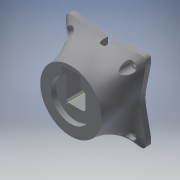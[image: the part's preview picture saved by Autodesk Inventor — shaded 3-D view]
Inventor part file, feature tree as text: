
AUTODESK INVENTOR PART (.ipt)
format: ipt  version: 2018 (Build 220112000, 112)  size: 1,945,600 bytes
history: native  units: mm
features: sketch x37, projected_geometry x36, extrude x32, fillet x13, hole x4, chamfer x4, mirror x1, other x1, revolve x1, shell x1, pattern_circular x1
ambient origin geometry x8: Origin, YZ Plane, XZ Plane, XY Plane, X Axis, Y Axis, Z Axis, Center Point
bodies: Solid1 (feature_tree)
feature tree (131):
  extrude  "Extrusion1"  Depth=45.0mm
  extrude  "Extrusion2"  Depth=2.25mm
  hole  "Hole1"  [1 undecoded]
  hole  "Hole2"  [1 undecoded]
  fillet  "Fillet1"  Radius=14.0mm
  extrude  "Extrusion3"  Depth=18.5mm
  extrude  "Extrusion4"  Depth=10.0mm
  extrude  "Extrusion5"  Depth=2.195mm
  extrude  "Extrusion6"  Depth=20.5mm
  hole  "Hole3"  [1 undecoded]
  extrude  "Extrusion7"  Depth=0.5mm
  extrude  "Extrusion8"  Depth=5.0mm TaperAngle=0.0deg
  extrude  "Extrusion9"  Depth=10.0mm
  extrude  "Extrusion10"  Depth=10.0mm
  extrude  "Extrusion11"  Depth=14.5mm
  extrude  "Extrusion12"  Depth=14.5mm
  extrude  "Extrusion13"  Depth=5.0mm
  extrude  "Extrusion14"  Depth=2.25mm
  extrude  "Extrusion15"  Depth=5.0mm
  extrude  "Extrusion16"  Depth=9.0mm
  extrude  "Extrusion17"  Depth=4.0mm
  chamfer  "Chamfer1"  Distance=1.0mm
  fillet  "Fillet7"  Radius=20.7mm
  fillet  "Fillet8"  Radius=32.0mm
  mirror  "Mirror1"
  extrude  "Extrusion18"  Depth=1.0mm TaperAngle=0.0deg
  extrude  "Extrusion19"  Depth=8.0mm
  extrude  "Extrusion20"  Depth=0.2mm TaperAngle=0.0deg
  extrude  "Extrusion21"  Depth=0.5mm TaperAngle=0.0deg
  extrude  "Extrusion22"  Depth=3.0mm TaperAngle=0.0deg
  extrude  "Extrusion23"  Depth=0.2mm TaperAngle=0.0deg
  extrude  "Extrusion24"  Depth=2.5mm TaperAngle=45.0deg
  sketch  "Sketch35"  dims[d91=8.0mm d92=0.0mm d93=3.0mm d94=0.0mm]
  other  "Work Axis1"
  revolve  "Revolution1"  [1 undecoded]
  extrude  "Extrusion25"  Depth=4.0mm TaperAngle=0.0deg
  extrude  "Extrusion26"  Depth=19.2mm TaperAngle=0.0deg
  shell  "Shell1"  Thickness=52.1mm
  extrude  "Extrusion27"  Depth=9.0mm
  extrude  "Extrusion28"  Depth=25.0mm
  chamfer  "Chamfer4"  Distance=6.9mm
  chamfer  "Chamfer5"  Distance=5.2mm
  extrude  "Extrusion29"  Depth=5.2mm
  pattern_circular  "Circular Pattern1"  [2 undecoded]
  fillet  "Fillet11"  Radius=5.0mm
  fillet  "Fillet12"  [1 undecoded]
  fillet  "Fillet13"  Radius=5.0mm
  fillet  "Fillet14"  Radius=105.0mm
  chamfer  "Chamfer6"  Distance=105.0mm
  hole  "Hole6"  [1 undecoded]
  extrude  "Extrusion30"  Depth=0.3mm
  fillet  "Fillet15"  Radius=12.8mm
  extrude  "Extrusion31"  Depth=0.3mm
  fillet  "Fillet16"  Radius=12.8mm
  extrude  "Extrusion32"  Depth=0.3mm
  fillet  "Fillet17"  Radius=20.0mm
  fillet  "Fillet18"  Radius=20.0mm
  fillet  "Fillet19"  Radius=6.0mm
  fillet  "Fillet20"  Radius=40.0mm
  sketch  "Sketch1"  dims[d0=24.5mm d1=45.0mm]
  sketch  "Sketch2"  dims[d2=1.95mm d3=0.0mm d4=2.25mm]
  projected_geometry  "Projected Loop1"
  sketch  "Sketch3"  dims[d5=20.0mm d6=2.25mm]
  projected_geometry  "Projected Loop2"
  sketch  "Sketch4"  dims[d7=5.25mm d8=5.25mm d9=14.0mm]
  projected_geometry  "Projected Loop3"
  sketch  "Sketch5"  dims[d10=5.25mm d11=18.5mm]
  projected_geometry  "Projected Loop4"
  sketch  "Sketch6"  dims[d12=10.0mm d13=0.0mm d14=20.5mm]
  projected_geometry  "Projected Loop5"
  sketch  "Sketch7"  dims[d15=2.0mm d16=2.195mm]
  projected_geometry  "Projected Loop6"
  sketch  "Sketch8"  dims[d17=2.0mm]
  projected_geometry  "Projected Loop7"
  sketch  "Sketch9"  dims[d18=2.4mm d19=6.0mm d20=4.4mm d21=2.0mm d22=90.0deg d23=8.0mm d24=20.594885mm d25=20.5mm]
  projected_geometry  "Projected Loop8"
  projected_geometry  "Projected Loop9"
  sketch  "Sketch10"  dims[d26=26.65mm d27=2.0mm]
  projected_geometry  "Projected Loop10"
  projected_geometry  "Projected Loop11"
  sketch  "Sketch11"  dims[d28=2.0mm]
  projected_geometry  "Projected Loop12"
  sketch  "Sketch12"  dims[d29=2.4mm d30=6.0mm d31=4.4mm d32=2.0mm d33=90.0deg d34=8.0mm d35=20.594885mm d36=0.5mm]
  sketch  "Sketch13"  dims[d37=18.0mm d38=5.0mm d39=0.0mm]
  sketch  "Sketch14"  dims[d41=10.0mm d42=0.0mm d43=24.5mm]
  projected_geometry  "Projected Loop13"
  sketch  "Sketch15"  dims[d44=1.15mm d45=0.0mm d46=10.0mm]
  sketch  "Sketch16"  dims[d47=21.0mm d48=14.5mm]
  projected_geometry  "Projected Loop14"
  sketch  "Sketch17"  dims[d49=20.0mm d50=14.5mm]
  projected_geometry  "Projected Loop15"
  sketch  "Sketch18"  dims[d51=24.5mm d52=5.0mm]
  projected_geometry  "Projected Loop16"
  sketch  "Sketch19"  dims[d53=5.0mm d54=2.25mm]
  projected_geometry  "Projected Loop17"
  sketch  "Sketch20"  dims[d55=2.25mm d56=5.0mm]
  projected_geometry  "Projected Loop18"
  sketch  "Sketch22"  dims[d57=5.0mm d58=9.0mm]
  sketch  "Sketch25"  dims[d59=14.75mm d60=4.0mm d61=1.0mm d62=0.0mm d63=20.7mm]
  sketch  "Sketch27"  dims[d64=2.4mm d65=6.0mm d66=4.4mm d67=2.0mm d68=90.0deg d69=8.0mm d70=20.594885mm d72=32.0mm]
  projected_geometry  "Projected Loop22"
  sketch  "Sketch28"  dims[d73=5.0mm d74=0.0mm d75=1.0mm d76=0.0mm]
  projected_geometry  "Projected Loop23"
  sketch  "Sketch29"  dims[d77=12.25mm d78=0.0mm d80=8.0mm]
  projected_geometry  "Projected Loop24"
  sketch  "Sketch30"  dims[d81=4.5mm d82=0.0mm d84=0.2mm d85=0.0mm]
  projected_geometry  "Projected Loop25"
  sketch  "Sketch33"  dims[d86=21.0mm d87=0.5mm d88=0.0mm]
  projected_geometry  "Projected Loop26"
  sketch  "Sketch36"  dims[d95=5.0mm d96=0.0mm d98=0.2mm d99=0.0mm]
  projected_geometry  "Projected Loop27"
  sketch  "Sketch37"  dims[d100=0.2mm d101=0.0mm d102=2.5mm d103=2.0mm d104=45.0deg]
  projected_geometry  "Projected Loop28"
  sketch  "Sketch38"  dims[d105=1.5mm d114=0.5mm]
  projected_geometry  "Projected Loop29"
  projected_geometry  "Projected Loop30"
  projected_geometry  "Projected Loop31"
  projected_geometry  "Projected Loop32"
  sketch  "Sketch39"  dims[d115=22.55mm d116=0.0mm d128=4.0mm d129=0.0mm]
  projected_geometry  "Projected Loop33"
  projected_geometry  "Projected Loop34"
  sketch  "Sketch40"  dims[d130=4.0mm d131=0.0mm d132=19.2mm d133=0.0mm d134=52.1mm]
  projected_geometry  "Projected Loop35"
  sketch  "Sketch41"  dims[d135=6.8mm d136=0.0mm d137=9.0mm]
  projected_geometry  "Projected Loop36"
  sketch  "Sketch42"  dims[d138=9.0mm d139=25.0mm d140=6.9mm d141=0.0mm]
  sketch  "Sketch43"  dims[d142=5.2mm]
  projected_geometry  "Projected Loop37"
  sketch  "Sketch44"  dims[d143=5.2mm d144=5.2mm d145=5.2mm d146=2.5mm d147=0.0mm d148=5.0mm d149=90.0deg d150=5.0mm d151=105.0mm d152=105.0mm d153=5.0mm d154=0.0mm d156=12.8mm d157=12.8mm d158=12.8mm d159=12.8mm d160=20.0mm d161=20.0mm d162=20.0mm d163=6.0mm d164=40.0mm d165=0.0mm d166=8.0mm d167=40.0mm d168=0.0mm d169=40.0mm d170=0.0mm d178=5.1mm d179=2.45mm d180=45.0deg d181=4.1mm d182=2.45mm d183=45.0deg d184=10.0mm d185=10.0mm d186=40.0mm d187=0.0mm d188=40.0mm d189=360.0deg d191=5.1mm d192=25.0mm d193=50.0mm d194=50.0mm d195=5.0mm d196=2.0mm d197=45.0deg d198=110.0mm d199=77.781746mm d200=77.781746mm d201=6.4mm d202=6.0mm d203=12.6mm d204=2.0mm d205=90.0deg d206=8.0mm d207=20.594885mm d208=11.0mm d209=11.0mm d210=11.0mm d211=11.0mm d212=45.0mm d213=0.0mm d214=1.0mm d215=2.0mm d216=0.0mm d217=1.5mm d218=8.0mm d219=12.0mm d220=12.0mm d221=0.0mm d222=2.0mm d223=5.0mm d224=2.0mm d225=0.3mm]
  projected_geometry  "Projected Loop38"
  projected_geometry  "Project Cut Edges1"
note: 8 required parameter values undecoded (feature->parameter linkage not recoverable at this tier; creation-order binding heuristic only, values carry confidence <= 0.55)